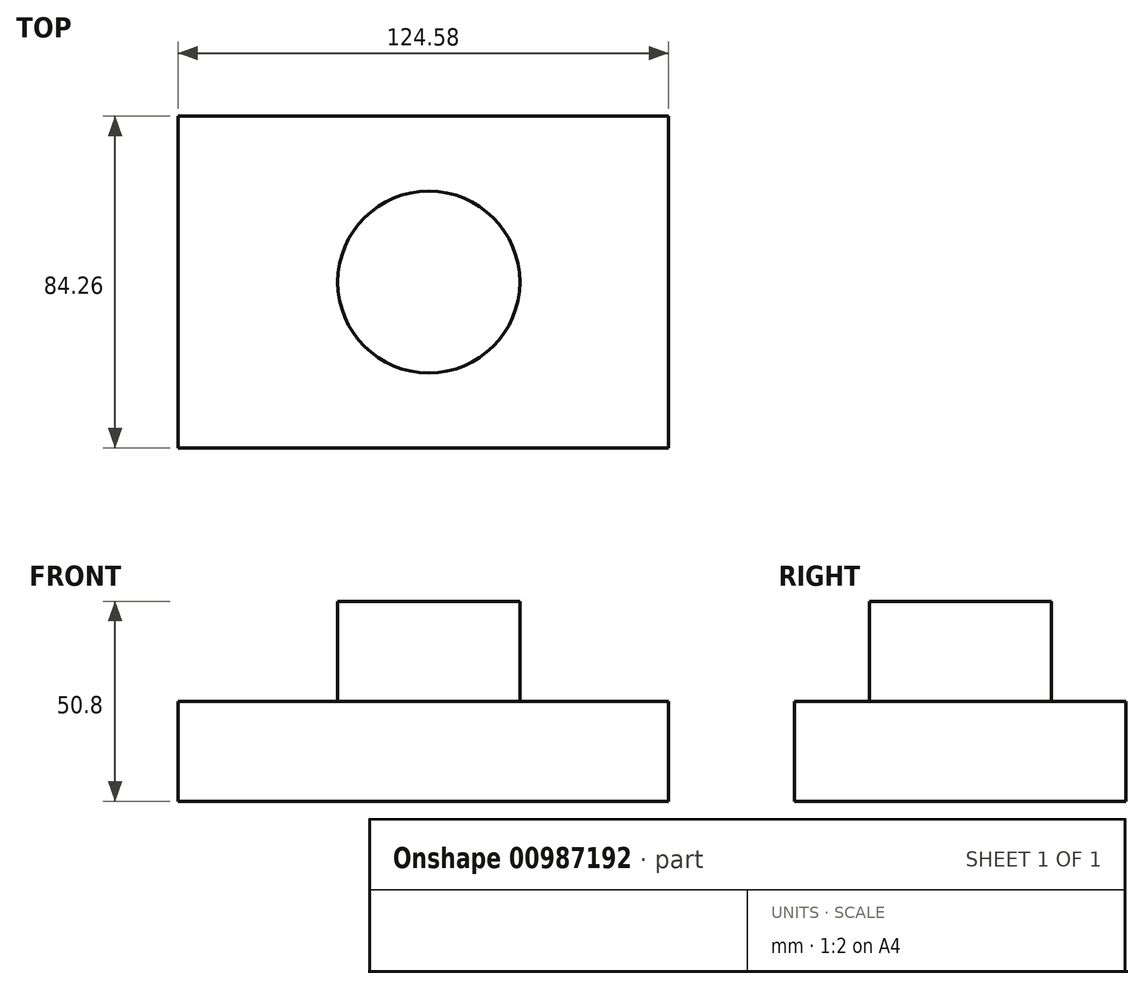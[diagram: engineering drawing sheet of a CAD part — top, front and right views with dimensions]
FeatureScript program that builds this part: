
annotation { "Feature Type Name" : "Feature", "Feature Type Description" : "" }
export const myFeature = defineFeature(function(context is Context, id is Id, definition is map)
    precondition{}
    {
        {
            var Q0;
            Q0=qCreatedBy(makeId("Top.planeOp"),FACE);
            var sketch = newSketch(context, id + "F0", { "sketchPlane" : qUnion([Q0])});
            skLineSegment(sketch, "E0.bottom", {"start": v(62.3, -42.13) * mm, "end": v(-62.3, -42.13) * mm});
            skLineSegment(sketch, "E0.top", {"start": v(62.3, 42.13) * mm, "end": v(-62.3, 42.13) * mm});
            skLineSegment(sketch, "E0.left", {"start": v(62.3, -42.13) * mm, "end": v(62.3, 42.13) * mm});
            skLineSegment(sketch, "E0.right", {"start": v(-62.3, -42.13) * mm, "end": v(-62.3, 42.13) * mm});
            skPoint(sketch, "E0.middle", {"position": v(0, 0) * mm});
            skSolve(sketch);
        }
        {
            var Q0;
            Q0=makeQuery(id+"F0.imprint","IMPRINT",FACE,{"disambiguationData":[TD([[makeQuery(id+"F0.imprint","IMPRINT",EDGE,{"derivedFrom":sQuery(id+"F0.wireOp",EDGE,"E0.bottom")}),-1.0]])]});
            extrude(context, id + "F1", {"entities" : qUnion([Q0]), "depth" : 25.4 * mm, "offsetDistance" : 25.4 * mm});
        }
        {
            var Q0;
            Q0=makeQuery(id+"F1.opExtrude","CAP_FACE",FACE,{"disambiguationData":[OSD([sQuery(id+"F0.wireOp",EDGE,"E0.bottom"),sQuery(id+"F0.wireOp",EDGE,"E0.top"),sQuery(id+"F0.wireOp",EDGE,"E0.left"),sQuery(id+"F0.wireOp",EDGE,"E0.right")])],"isStart":false});
            var sketch = newSketch(context, id + "F2", { "sketchPlane" : qUnion([Q0])});
            skCircle(sketch, "E1", {"center": v(1.4, 0) * mm, "radius": 23.12 * mm});
            skSolve(sketch);
        }
        {
            var Q0;
            Q0=qSketchRegion(id+"F2",true);
            extrude(context, id + "F3", {"entities" : qUnion([Q0]), "operationType" : NewBodyOperationType.ADD, "depth" : 25.4 * mm, "offsetDistance" : 25.4 * mm});
        }
    });
